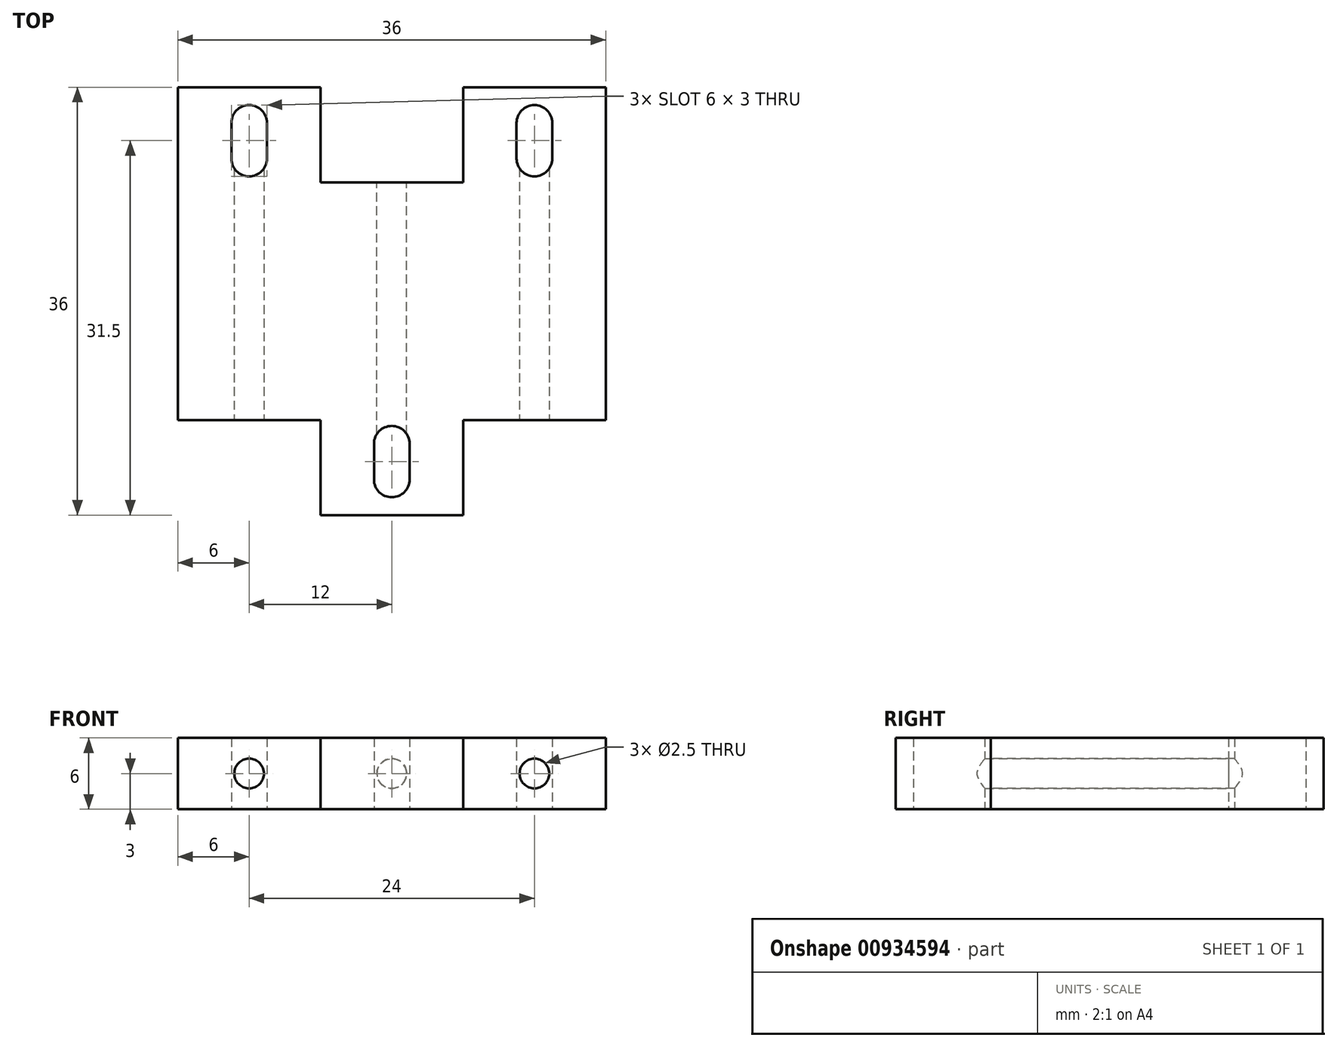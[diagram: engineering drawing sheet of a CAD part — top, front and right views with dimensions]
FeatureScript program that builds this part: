
annotation { "Feature Type Name" : "Feature", "Feature Type Description" : "" }
export const myFeature = defineFeature(function(context is Context, id is Id, definition is map)
    precondition{}
    {
        {
            var Q0;
            Q0=qCreatedBy(makeId("Top.planeOp"),FACE);
            var sketch = newSketch(context, id + "F0", { "sketchPlane" : qUnion([Q0])});
            skLineSegment(sketch, "E0.bottom", {"start": v(6, -18) * mm, "end": v(-6, -18) * mm});
            skLineSegment(sketch, "E0.top", {"start": v(18, 18) * mm, "end": v(6, 18) * mm});
            skLineSegment(sketch, "E0.left", {"start": v(18, -10) * mm, "end": v(18, 18) * mm});
            skLineSegment(sketch, "E0.right", {"start": v(-18, -10) * mm, "end": v(-18, 18) * mm});
            skPoint(sketch, "E0.middle", {"position": v(0, 0) * mm});
            skLineSegment(sketch, "E1", {"start": v(-6, 18) * mm, "end": v(-6, 10) * mm});
            skLineSegment(sketch, "E2", {"start": v(6, 18) * mm, "end": v(6, 10) * mm});
            skLineSegment(sketch, "E3", {"start": v(-6, 10) * mm, "end": v(6, 10) * mm});
            skLineSegment(sketch, "E4", {"start": v(-18, -10) * mm, "end": v(-6, -10) * mm});
            skPoint(sketch, "E5.orphan", {"position": v(-18, 10) * mm});
            skLineSegment(sketch, "E6.trimOffspring", {"start": v(-6, 18) * mm, "end": v(-18, 18) * mm});
            skPoint(sketch, "E7.orphan", {"position": v(-18, -18) * mm});
            skPoint(sketch, "E8.orphan", {"position": v(18, -18) * mm});
            skLineSegment(sketch, "E9.trimOffspring", {"start": v(6, -10) * mm, "end": v(18, -10) * mm});
            skLineSegment(sketch, "E10.trimOffspring", {"start": v(-6, -10) * mm, "end": v(-6, -18) * mm});
            skLineSegment(sketch, "E11.trimOffspring", {"start": v(6, -10) * mm, "end": v(6, -18) * mm});
            skLineSegment(sketch, "E12", {"start": v(-12, 18) * mm, "end": v(-12, -10) * mm, "construction": true});
            skArc(sketch, "E13", {"start": v(-10.5, 15) * mm, "mid": v(-12, 16.5) * mm, "end": v(-13.5, 15) * mm});
            skArc(sketch, "E14", {"start": v(-13.5, 12) * mm, "mid": v(-12, 10.5) * mm, "end": v(-10.5, 12) * mm});
            skLineSegment(sketch, "E15", {"start": v(-13.5, 15) * mm, "end": v(-13.5, 12) * mm});
            skLineSegment(sketch, "E16", {"start": v(-10.5, 15) * mm, "end": v(-10.5, 12) * mm});
            skArc(sketch, "E17.MirrorCS", {"start": v(10.5, 15) * mm, "mid": v(12, 16.5) * mm, "end": v(13.5, 15) * mm});
            skLineSegment(sketch, "E18.MirrorCS", {"start": v(13.5, 15) * mm, "end": v(13.5, 12) * mm});
            skLineSegment(sketch, "E19.MirrorCS", {"start": v(10.5, 15) * mm, "end": v(10.5, 12) * mm});
            skArc(sketch, "E20.MirrorCS", {"start": v(13.5, 12) * mm, "mid": v(12, 10.5) * mm, "end": v(10.5, 12) * mm});
            skLineSegment(sketch, "E21.MirrorCS", {"start": v(1.5, -15) * mm, "end": v(1.5, -12) * mm});
            skArc(sketch, "E22.MirrorCS", {"start": v(-1.5, -12) * mm, "mid": v(0, -10.5) * mm, "end": v(1.5, -12) * mm});
            skLineSegment(sketch, "E23.MirrorCS", {"start": v(-1.5, -15) * mm, "end": v(-1.5, -12) * mm});
            skArc(sketch, "E24.MirrorCS", {"start": v(1.5, -15) * mm, "mid": v(0, -16.5) * mm, "end": v(-1.5, -15) * mm});
            skSolve(sketch);
        }
        {
            var Q0;
            Q0 = qSketchRegion(id + "F0", true);
            extrude(context, id + "F1", {"entities" : qUnion([Q0]), "depth" : 6 * mm, "offsetDistance" : 25 * mm});
        }
        {
            var Q0;
            Q0=makeQuery(id+"F0.imprint","IMPRINT",FACE,{"disambiguationData":[TD([[makeQuery(id+"F0.imprint","IMPRINT",EDGE,{"derivedFrom":sQuery(id+"F0.wireOp",EDGE,"E0.bottom")}),-1.0]])]});
            extrude(context, id + "F2", {"entities" : qUnion([Q0]), "operationType" : NewBodyOperationType.ADD, "depth" : 6 * mm, "offsetDistance" : 25 * mm});
        }
        {
            var Q0;
            Q0=makeQuery(id+"F1.opExtrude","SWEPT_FACE",FACE,{"disambiguationData":[OSD([sQuery(id+"F0.wireOp",EDGE,"E4")])]});
            var sketch = newSketch(context, id + "F3", { "sketchPlane" : qUnion([Q0])});
            skLineSegment(sketch, "E25", {"start": v(-12, 6) * mm, "end": v(-12, 0) * mm, "construction": true});
            skCircle(sketch, "E26", {"center": v(-12, 3) * mm, "radius": 1.25 * mm});
            skCircle(sketch, "E27.MirrorC", {"center": v(12, 3) * mm, "radius": 1.25 * mm});
            skSolve(sketch);
        }
        {
            var Q0;
            Q0 = qSketchRegion(id + "F3", true);
            extrude(context, id + "F4", {"entities" : qUnion([Q0]), "operationType" : NewBodyOperationType.REMOVE, "endBound" : BoundingType.UP_TO_NEXT, "oppositeDirection" : true, "depth" : 25 * mm, "offsetDistance" : 25 * mm});
        }
        {
            var Q0;
            Q0=makeQuery(id+"F1.opExtrude","SWEPT_FACE",FACE,{"disambiguationData":[OSD([sQuery(id+"F0.wireOp",EDGE,"E3")])]});
            var sketch = newSketch(context, id + "F5", { "sketchPlane" : qUnion([Q0])});
            skLineSegment(sketch, "E28", {"start": v(0, 0) * mm, "end": v(0, 6) * mm, "construction": true});
            skCircle(sketch, "E29", {"center": v(0, 3) * mm, "radius": 1.25 * mm});
            skSolve(sketch);
        }
        {
            var Q0;
            Q0 = qSketchRegion(id + "F5", true);
            extrude(context, id + "F6", {"entities" : qUnion([Q0]), "operationType" : NewBodyOperationType.REMOVE, "endBound" : BoundingType.UP_TO_NEXT, "oppositeDirection" : true, "depth" : 25 * mm, "offsetDistance" : 25 * mm});
        }
    });
